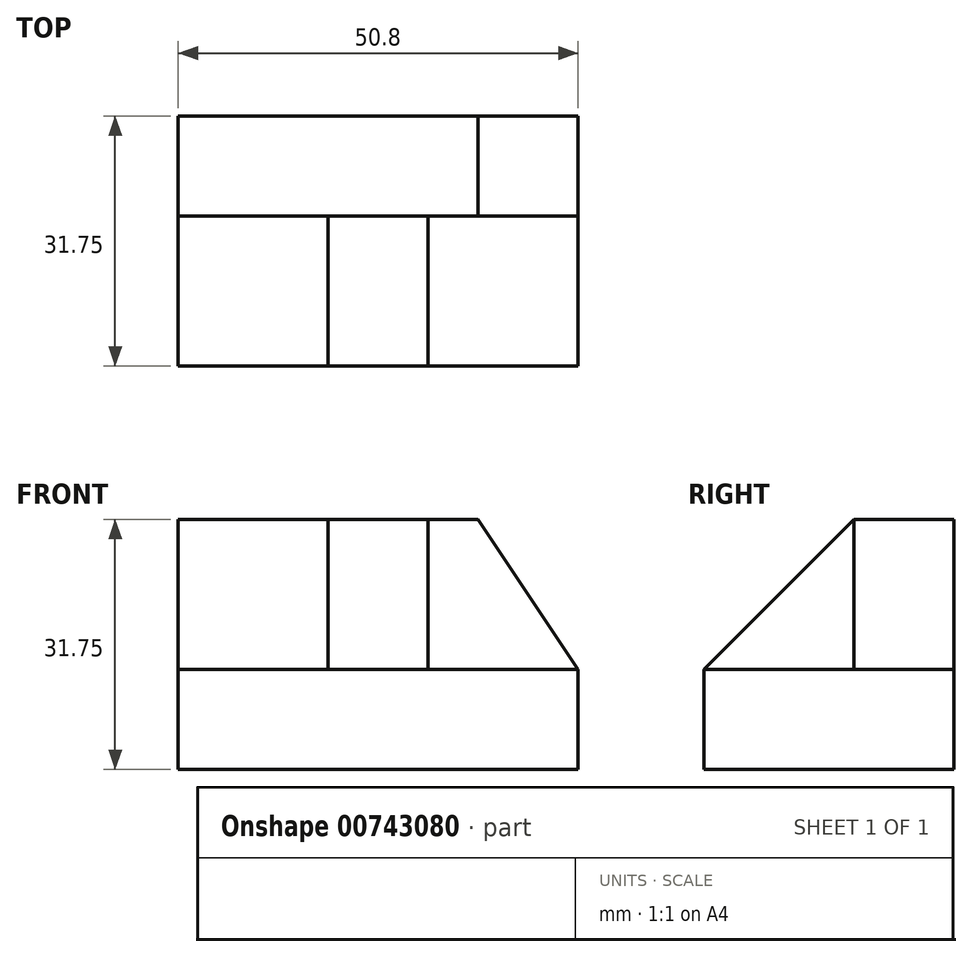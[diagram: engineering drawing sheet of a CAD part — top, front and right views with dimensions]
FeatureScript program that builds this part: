
annotation { "Feature Type Name" : "Feature", "Feature Type Description" : "" }
export const myFeature = defineFeature(function(context is Context, id is Id, definition is map)
    precondition{}
    {
        {
            var Q0;
            Q0=qCreatedBy(makeId("Front.planeOp"),FACE);
            var sketch = newSketch(context, id + "F0", { "sketchPlane" : qUnion([Q0])});
            skLineSegment(sketch, "E0", {"start": v(0, 0) * mm, "end": v(50.8, 0) * mm});
            skLineSegment(sketch, "E1", {"start": v(50.8, 0) * mm, "end": v(50.8, 31.75) * mm});
            skLineSegment(sketch, "E2", {"start": v(50.8, 31.75) * mm, "end": v(0, 31.75) * mm});
            skLineSegment(sketch, "E3", {"start": v(0, 31.75) * mm, "end": v(0, 0) * mm});
            skSolve(sketch);
        }
        {
            var Q0;
            Q0=makeQuery(id+"F0.imprint","IMPRINT",FACE,{"disambiguationData":[TD([[makeQuery(id+"F0.imprint","IMPRINT",EDGE,{"derivedFrom":sQuery(id+"F0.wireOp",EDGE,"E0")}),1.0]])]});
            extrude(context, id + "F1", {"entities" : qUnion([Q0]), "depth" : 31.75 * mm, "offsetDistance" : 25.4 * mm});
        }
        {
            var Q0;
            Q0=makeQuery(id+"F1.opExtrude","SWEPT_FACE",FACE,{"disambiguationData":[OSD([sQuery(id+"F0.wireOp",EDGE,"E3")])]});
            var sketch = newSketch(context, id + "F2", { "sketchPlane" : qUnion([Q0])});
            skLineSegment(sketch, "E4", {"start": v(12.7, 31.75) * mm, "end": v(12.7, 12.7) * mm});
            skLineSegment(sketch, "E5", {"start": v(12.7, 12.7) * mm, "end": v(31.75, 12.7) * mm});
            skSolve(sketch);
        }
        {
            var Q0;
            {var subQ0=sQuery(id+"F2.wireOp",EDGE,"E4");Q0=makeQuery(id+"F2.imprint","IMPRINT",FACE,{"disambiguationData":[TD([[makeQuery(id+"F2.imprint","IMPRINT",EDGE,{"derivedFrom":subQ0}),1.0]])]});}
            extrude(context, id + "F3", {"entities" : qUnion([Q0]), "operationType" : NewBodyOperationType.REMOVE, "oppositeDirection" : true, "depth" : 19.05 * mm, "offsetDistance" : 25.4 * mm});
        }
        {
            var Q0;
            Q0=makeQuery(id+"F1.opExtrude","SWEPT_FACE",FACE,{"disambiguationData":[OSD([sQuery(id+"F0.wireOp",EDGE,"E1")])]});
            var sketch = newSketch(context, id + "F4", { "sketchPlane" : qUnion([Q0])});
            skLineSegment(sketch, "E6", {"start": v(-31.75, 12.7) * mm, "end": v(-12.7, 12.7) * mm});
            skLineSegment(sketch, "E7", {"start": v(-12.7, 12.7) * mm, "end": v(-12.7, 31.75) * mm});
            skSolve(sketch);
        }
        {
            var Q0;
            {var subQ0=sQuery(id+"F4.wireOp",EDGE,"E6");Q0=makeQuery(id+"F4.imprint","IMPRINT",FACE,{"disambiguationData":[TD([[makeQuery(id+"F4.imprint","IMPRINT",EDGE,{"derivedFrom":subQ0}),1.0]])]});}
            extrude(context, id + "F5", {"entities" : qUnion([Q0]), "operationType" : NewBodyOperationType.REMOVE, "oppositeDirection" : true, "depth" : 19.05 * mm, "offsetDistance" : 25.4 * mm});
        }
        {
            var Q0;
            Q0=makeQuery(id+"F5.boolean.opBoolean","COPY",FACE,{"derivedFrom":makeQuery(id+"F5.opExtrude","CAP_FACE",FACE,{"disambiguationData":[OSD([sQuery(id+"F0.wireOp",EDGE,"E1"),sQuery(id+"F0.wireOp",EDGE,"E2"),sQuery(id+"F4.wireOp",EDGE,"E6"),sQuery(id+"F4.wireOp",EDGE,"E7")])],"isStart":false})});
            var sketch = newSketch(context, id + "F6", { "sketchPlane" : qUnion([Q0])});
            skLineSegment(sketch, "E8", {"start": v(-31.75, 12.7) * mm, "end": v(-12.7, 31.75) * mm});
            skSolve(sketch);
        }
        {
            var Q0;
            Q0=makeQuery(id+"F6.imprint","IMPRINT",FACE,{"disambiguationData":[TD([[makeQuery(id+"F6.imprint","IMPRINT",EDGE,{"derivedFrom":sQuery(id+"F6.wireOp",EDGE,"E8")}),1.0]])]});
            extrude(context, id + "F7", {"entities" : qUnion([Q0]), "operationType" : NewBodyOperationType.REMOVE, "oppositeDirection" : true, "depth" : 25.4 * mm, "offsetDistance" : 25.4 * mm});
        }
        {
            var Q0;
            Q0=makeQuery(id+"F5.boolean.opBoolean","COPY",FACE,{"derivedFrom":makeQuery(id+"F5.opExtrude","SWEPT_FACE",FACE,{"disambiguationData":[OSD([sQuery(id+"F4.wireOp",EDGE,"E7")])]})});
            var sketch = newSketch(context, id + "F8", { "sketchPlane" : qUnion([Q0])});
            skLineSegment(sketch, "E9", {"start": v(38.1, 31.75) * mm, "end": v(50.8, 12.7) * mm});
            skSolve(sketch);
        }
        {
            var Q0;
            {var subQ0=sQuery(id+"F8.wireOp",EDGE,"E9");Q0=makeQuery(id+"F8.imprint","IMPRINT",FACE,{"disambiguationData":[TD([[makeQuery(id+"F8.imprint","IMPRINT",EDGE,{"derivedFrom":subQ0}),1.0]])]});}
            extrude(context, id + "F9", {"entities" : qUnion([Q0]), "operationType" : NewBodyOperationType.REMOVE, "oppositeDirection" : true, "depth" : 25.4 * mm, "offsetDistance" : 25.4 * mm});
        }
    });
